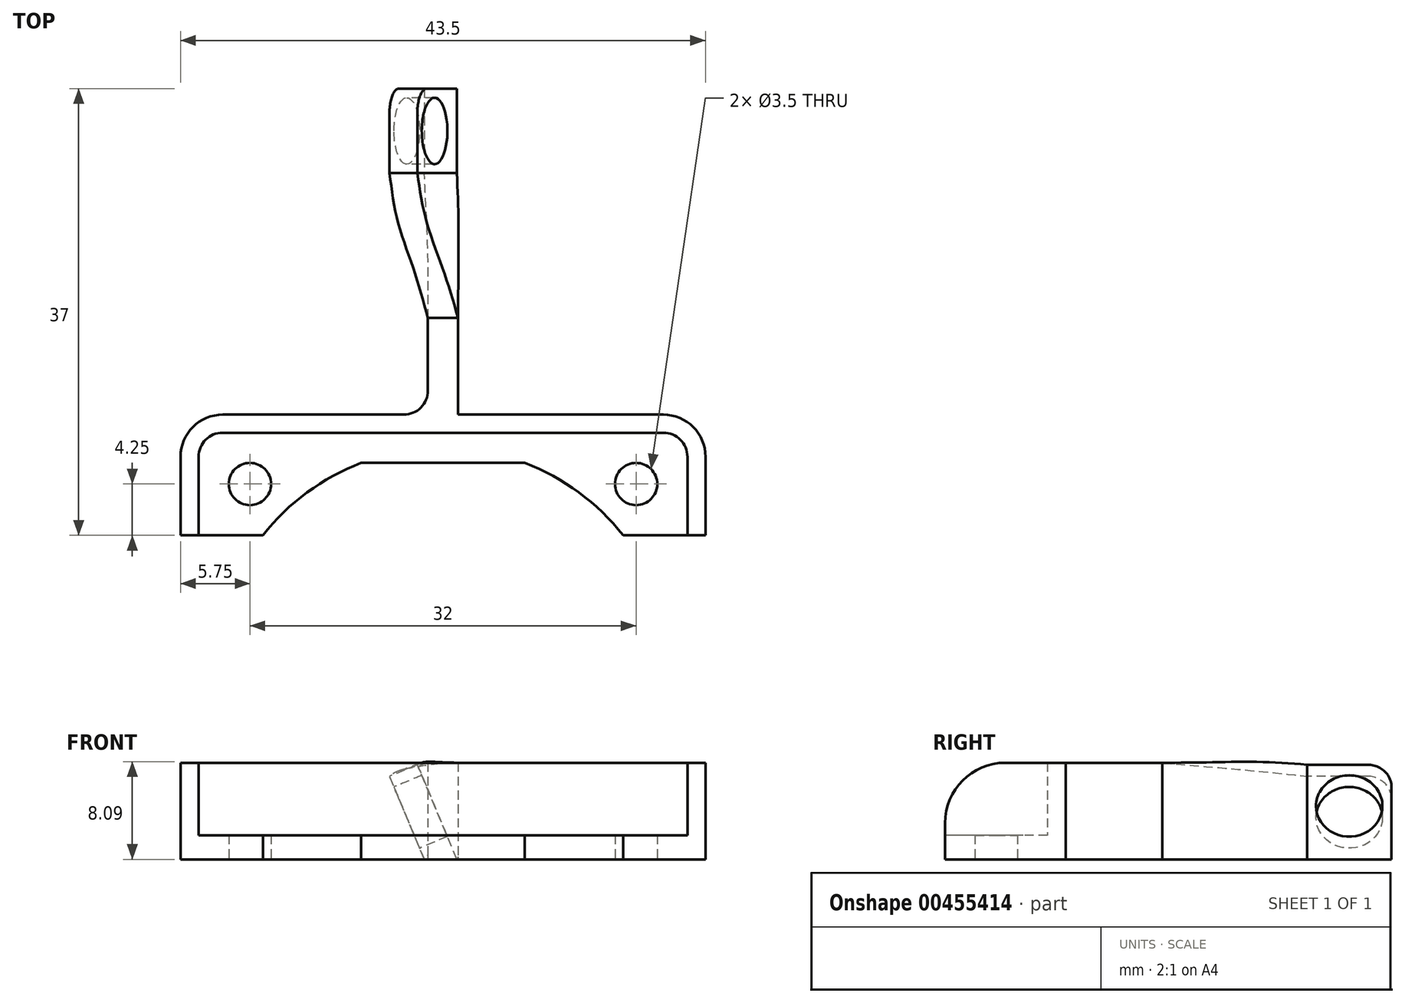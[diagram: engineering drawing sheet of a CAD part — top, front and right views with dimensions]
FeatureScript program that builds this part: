
annotation { "Feature Type Name" : "Feature", "Feature Type Description" : "" }
export const myFeature = defineFeature(function(context is Context, id is Id, definition is map)
    precondition{}
    {
        {
            var Q0;
            Q0=qCreatedBy(makeId("Top.planeOp"),FACE);
            var sketch = newSketch(context, id + "F0", { "sketchPlane" : qUnion([Q0])});
            skCircle(sketch, "E0", {"center": v(0, 0) * mm, "radius": 1.75 * mm});
            skCircle(sketch, "E1", {"center": v(32, 0) * mm, "radius": 1.75 * mm});
            skLineSegment(sketch, "E2", {"start": v(-4.25, 4.25) * mm, "end": v(-4.25, -4.25) * mm});
            skLineSegment(sketch, "E3", {"start": v(36.25, 4.25) * mm, "end": v(36.25, -4.25) * mm});
            skLineSegment(sketch, "E4", {"start": v(-4.25, 4.25) * mm, "end": v(36.25, 4.25) * mm});
            skLineSegment(sketch, "E5", {"start": v(-4.25, -4.25) * mm, "end": v(1.07, -4.25) * mm});
            skLineSegment(sketch, "E6", {"start": v(30.93, -4.25) * mm, "end": v(36.25, -4.25) * mm});
            skArc(sketch, "E7", {"start": v(30.93, -4.25) * mm, "mid": v(27.26, -0.7) * mm, "end": v(22.78, 1.75) * mm});
            skPoint(sketch, "E8.orphan", {"position": v(5.05, -4.25) * mm});
            skPoint(sketch, "E9.orphan", {"position": v(25.59, -4.25) * mm});
            skLineSegment(sketch, "E10", {"start": v(9.22, 1.75) * mm, "end": v(22.78, 1.75) * mm});
            skArc(sketch, "E11.trimOffspring", {"start": v(9.22, 1.75) * mm, "mid": v(4.74, -0.7) * mm, "end": v(1.07, -4.25) * mm});
            skSolve(sketch);
        }
        {
            var Q0;
            Q0=makeQuery(id+"F0.imprint","IMPRINT",FACE,{"disambiguationData":[TD([[makeQuery(id+"F0.imprint","IMPRINT",EDGE,{"derivedFrom":sQuery(id+"F0.wireOp",EDGE,"E0")}),-1.0]])]});
            extrude(context, id + "F1", {"entities" : qUnion([Q0]), "depth" : 2 * mm});
        }
        {
            var Q0;
            Q0=makeQuery(id+"F1.opExtrude","SWEPT_EDGE",EDGE,{"disambiguationData":[OSD([sQuery(id+"F0.wireOp",EDGE,"E3"),sQuery(id+"F0.wireOp",EDGE,"E4")])]});
            var Q1;
            Q1=makeQuery(id+"F1.opExtrude","SWEPT_EDGE",EDGE,{"disambiguationData":[OSD([sQuery(id+"F0.wireOp",EDGE,"E2"),sQuery(id+"F0.wireOp",EDGE,"E4")])]});
            fillet(context, id + "F2", {"entities" : qUnion([Q0, Q1]), "radius" : 2 * mm, "tangentPropagation" : true, "allowEdgeOverflow" : false});
        }
        {
            var Q0;
            Q0=qCreatedBy(makeId("Top.planeOp"),FACE);
            var sketch = newSketch(context, id + "F3", { "sketchPlane" : qUnion([Q0])});
            skLineSegment(sketch, "E12.0", {"start": v(-5.75, 2.25) * mm, "end": v(-5.75, -4.25) * mm});
            skLineSegment(sketch, "E12.1", {"start": v(37.75, 2.25) * mm, "end": v(37.75, -4.25) * mm});
            skArc(sketch, "E12.2", {"start": v(37.75, 2.25) * mm, "mid": v(36.72, 4.72) * mm, "end": v(34.25, 5.75) * mm});
            skLineSegment(sketch, "E12.3", {"start": v(-2.25, 5.75) * mm, "end": v(34.25, 5.75) * mm});
            skArc(sketch, "E12.4", {"start": v(-2.25, 5.75) * mm, "mid": v(-4.72, 4.72) * mm, "end": v(-5.75, 2.25) * mm});
            skLineSegment(sketch, "E13.0", {"start": v(-4.25, 2.25) * mm, "end": v(-4.25, -4.25) * mm});
            skLineSegment(sketch, "E13.1", {"start": v(36.25, 2.25) * mm, "end": v(36.25, -4.25) * mm});
            skArc(sketch, "E13.2", {"start": v(36.25, 2.25) * mm, "mid": v(35.66, 3.66) * mm, "end": v(34.25, 4.25) * mm});
            skLineSegment(sketch, "E13.3", {"start": v(-2.25, 4.25) * mm, "end": v(34.25, 4.25) * mm});
            skArc(sketch, "E13.4", {"start": v(-2.25, 4.25) * mm, "mid": v(-3.66, 3.66) * mm, "end": v(-4.25, 2.25) * mm});
            skLineSegment(sketch, "E14", {"start": v(-5.75, -4.25) * mm, "end": v(-4.25, -4.25) * mm});
            skLineSegment(sketch, "E15", {"start": v(36.25, -4.25) * mm, "end": v(37.75, -4.25) * mm});
            skSolve(sketch);
        }
        {
            var Q0;
            Q0=makeQuery(id+"F3.imprint","IMPRINT",FACE,{"disambiguationData":[TD([[makeQuery(id+"F3.imprint","IMPRINT",EDGE,{"derivedFrom":sQuery(id+"F3.wireOp",EDGE,"E12.0")}),1.0]])]});
            extrude(context, id + "F4", {"entities" : qUnion([Q0]), "operationType" : NewBodyOperationType.ADD, "depth" : 8 * mm});
        }
        {
            var Q0;
            Q0=makeQuery(id+"F4.opExtrude","SWEPT_FACE",FACE,{"disambiguationData":[OSD([sQuery(id+"F3.wireOp",EDGE,"E12.1")])]});
            var Q1;
            Q1=makeQuery(id+"F4.opExtrude","SWEPT_FACE",FACE,{"disambiguationData":[OSD([sQuery(id+"F3.wireOp",EDGE,"E12.0")])]});
            cPlane(context, id + "F5", {"entities" : qUnion([Q0, Q1]), "cplaneType" : CPlaneType.MID_PLANE, "offset" : 25 * mm, "width" : 150 * mm, "height" : 150 * mm});
        }
        {
            var Q0;
            Q0=makeQuery(id+"F4.opExtrude","CAP_EDGE",EDGE,{"disambiguationData":[OSD([sQuery(id+"F3.wireOp",EDGE,"E14")])],"isStart":false});
            var Q1;
            Q1=makeQuery(id+"F4.opExtrude","CAP_EDGE",EDGE,{"disambiguationData":[OSD([sQuery(id+"F3.wireOp",EDGE,"E15")])],"isStart":false});
            fillet(context, id + "F6", {"entities" : qUnion([Q0, Q1]), "radius" : 5 * mm, "tangentPropagation" : true, "allowEdgeOverflow" : false});
        }
        {
            var Q0;
            Q0=makeQuery(id+"F4.opExtrude","SWEPT_FACE",FACE,{"disambiguationData":[OSD([sQuery(id+"F3.wireOp",EDGE,"E12.3")])]});
            cPlane(context, id + "F7", {"entities" : qUnion([Q0]), "cplaneType" : CPlaneType.OFFSET, "offset" : 8 * mm, "width" : 150 * mm, "height" : 150 * mm});
        }
        {
            var Q0;
            Q0=makeQuery(id+"F4.opExtrude","SWEPT_FACE",FACE,{"disambiguationData":[OSD([sQuery(id+"F3.wireOp",EDGE,"E12.3")])]});
            var sketch = newSketch(context, id + "F8", { "sketchPlane" : qUnion([Q0])});
            skLineSegment(sketch, "E16.bottom", {"start": v(-17.25, 8) * mm, "end": v(-14.75, 8) * mm});
            skLineSegment(sketch, "E16.top", {"start": v(-17.25, 0) * mm, "end": v(-14.75, 0) * mm});
            skLineSegment(sketch, "E16.left", {"start": v(-17.25, 8) * mm, "end": v(-17.25, 0) * mm});
            skLineSegment(sketch, "E16.right", {"start": v(-14.75, 8) * mm, "end": v(-14.75, 0) * mm});
            skSolve(sketch);
        }
        {
            var Q0;
            Q0=makeQuery(id+"F8.imprint","IMPRINT",FACE,{"disambiguationData":[TD([[makeQuery(id+"F8.imprint","IMPRINT",EDGE,{"derivedFrom":sQuery(id+"F8.wireOp",EDGE,"E16.bottom")}),1.0]])]});
            extrude(context, id + "F9", {"entities" : qUnion([Q0]), "operationType" : NewBodyOperationType.ADD, "depth" : 8 * mm});
        }
        {
            var Q0;
            Q0=makeQuery(id+"F9.opExtrude","CAP_EDGE",EDGE,{"disambiguationData":[OSD([sQuery(id+"F8.wireOp",EDGE,"E16.right")])],"isStart":true});
            var Q1;
            Q1=makeQuery(id+"F9.opExtrude","CAP_EDGE",EDGE,{"disambiguationData":[OSD([sQuery(id+"F8.wireOp",EDGE,"E16.left")])],"isStart":true});
            fillet(context, id + "F10", {"entities" : qUnion([Q0, Q1]), "radius" : 2 * mm, "tangentPropagation" : true, "allowEdgeOverflow" : false});
        }
        {
            var Q0;
            Q0=qCreatedBy(id+"F7.planeOp",FACE);
            cPlane(context, id + "F11", {"entities" : qUnion([Q0]), "cplaneType" : CPlaneType.OFFSET, "offset" : 4 * mm, "width" : 150 * mm, "height" : 150 * mm});
        }
        {
            var Q0;
            Q0=qCreatedBy(id+"F11.planeOp",FACE);
            var sketch = newSketch(context, id + "F12", { "sketchPlane" : qUnion([Q0])});
            skLineSegment(sketch, "E17", {"start": v(-16.01, 8.03) * mm, "end": v(-17.27, 0) * mm});
            skLineSegment(sketch, "E18", {"start": v(-17.27, 0) * mm, "end": v(-14.77, 0) * mm});
            skLineSegment(sketch, "E19", {"start": v(-14.77, 0) * mm, "end": v(-13.57, 7.65) * mm});
            skLineSegment(sketch, "E20", {"start": v(-16.01, 8.03) * mm, "end": v(-13.57, 7.65) * mm});
            skSolve(sketch);
        }
        {
            var Q0;
            Q0=qCreatedBy(id+"F11.planeOp",FACE);
            cPlane(context, id + "F13", {"entities" : qUnion([Q0]), "cplaneType" : CPlaneType.OFFSET, "offset" : 4 * mm, "width" : 150 * mm, "height" : 150 * mm});
        }
        {
            var Q0;
            Q0=qCreatedBy(id+"F13.planeOp",FACE);
            var sketch = newSketch(context, id + "F14", { "sketchPlane" : qUnion([Q0])});
            skLineSegment(sketch, "E21", {"start": v(-17.28, 0) * mm, "end": v(-14.63, 8.08) * mm});
            skLineSegment(sketch, "E22", {"start": v(-14.63, 8.08) * mm, "end": v(-12.26, 7.3) * mm});
            skLineSegment(sketch, "E23", {"start": v(-12.26, 7.3) * mm, "end": v(-14.65, 0) * mm});
            skLineSegment(sketch, "E24", {"start": v(-17.28, 0) * mm, "end": v(-14.65, 0) * mm});
            skSolve(sketch);
        }
        {
            var Q0;
            Q0=qCreatedBy(id+"F13.planeOp",FACE);
            cPlane(context, id + "F15", {"entities" : qUnion([Q0]), "cplaneType" : CPlaneType.OFFSET, "offset" : 4 * mm, "width" : 150 * mm, "height" : 150 * mm});
        }
        {
            var Q0;
            Q0=qCreatedBy(id+"F15.planeOp",FACE);
            var sketch = newSketch(context, id + "F16", { "sketchPlane" : qUnion([Q0])});
            skLineSegment(sketch, "E25", {"start": v(-17.15, 0) * mm, "end": v(-13.87, 7.84) * mm});
            skLineSegment(sketch, "E26", {"start": v(-13.87, 7.84) * mm, "end": v(-11.57, 6.88) * mm});
            skLineSegment(sketch, "E27", {"start": v(-11.57, 6.88) * mm, "end": v(-14.44, 0) * mm});
            skLineSegment(sketch, "E28", {"start": v(-14.44, 0) * mm, "end": v(-17.15, 0) * mm});
            skSolve(sketch);
        }
        {
            var Q1;
            Q1=makeQuery(id+"F9.opExtrude","CAP_FACE",FACE,{"disambiguationData":[OSD([sQuery(id+"F8.wireOp",EDGE,"E16.bottom"),sQuery(id+"F8.wireOp",EDGE,"E16.top"),sQuery(id+"F8.wireOp",EDGE,"E16.left"),sQuery(id+"F8.wireOp",EDGE,"E16.right")])],"isStart":false});
            var Q2;
            Q2=makeQuery(id+"F12.imprint","IMPRINT",FACE,{"disambiguationData":[TD([[makeQuery(id+"F12.imprint","IMPRINT",EDGE,{"derivedFrom":sQuery(id+"F12.wireOp",EDGE,"E17")}),1.0]])]});
            var Q3;
            Q3=makeQuery(id+"F14.imprint","IMPRINT",FACE,{"disambiguationData":[TD([[makeQuery(id+"F14.imprint","IMPRINT",EDGE,{"derivedFrom":sQuery(id+"F14.wireOp",EDGE,"E21")}),-1.0]])]});
            var Q4;
            Q4=makeQuery(id+"F16.imprint","IMPRINT",FACE,{"disambiguationData":[TD([[makeQuery(id+"F16.imprint","IMPRINT",EDGE,{"derivedFrom":sQuery(id+"F16.wireOp",EDGE,"E25")}),-1.0]])]});
            loft(context, id + "F17", {"operationType" : NewBodyOperationType.ADD, "sheetProfilesArray" : [{ "sheetProfileEntities" : qUnion([Q1]) }, { "sheetProfileEntities" : qUnion([Q2]) }, { "sheetProfileEntities" : qUnion([Q3]) }, { "sheetProfileEntities" : qUnion([Q4]) }]});
        }
        {
            var Q0;
            Q0=makeQuery(id+"F17.opLoft","CAP_FACE",FACE,{"disambiguationData":[OSD([makeQuery(id+"F16.imprint","IMPRINT",FACE,{"disambiguationData":[TD([[makeQuery(id+"F16.imprint","IMPRINT",EDGE,{"derivedFrom":sQuery(id+"F16.wireOp",EDGE,"E25")}),-1.0]])]})])],"isStart":true});
            extrude(context, id + "F18", {"entities" : qUnion([Q0]), "operationType" : NewBodyOperationType.ADD, "depth" : 7 * mm});
        }
        {
            var Q0;
            Q0=makeQuery(id+"F18.opExtrude","CAP_EDGE",EDGE,{"disambiguationData":[OSD([sQuery(id+"F16.wireOp",EDGE,"E25"),sQuery(id+"F16.wireOp",EDGE,"E26"),sQuery(id+"F16.wireOp",EDGE,"E27")])],"isStart":false});
            fillet(context, id + "F19", {"entities" : qUnion([Q0]), "radius" : 2 * mm, "tangentPropagation" : true, "allowEdgeOverflow" : false});
        }
        {
            var Q0;
            Q0=makeQuery(id+"F18.opExtrude","SWEPT_FACE",FACE,{"disambiguationData":[OSD([sQuery(id+"F16.wireOp",EDGE,"E26"),sQuery(id+"F16.wireOp",EDGE,"E27"),sQuery(id+"F16.wireOp",EDGE,"E28")])]});
            var sketch = newSketch(context, id + "F20", { "sketchPlane" : qUnion([Q0])});
            skCircle(sketch, "E29", {"center": v(-29.25, -1.81) * mm, "radius": 2.75 * mm});
            skSolve(sketch);
        }
        {
            var Q0;
            Q0=sQuery(id+"F20.wireOp",VERTEX,"E29.center");
            var Q1;
            Q1=makeQuery(id+"F1.opExtrude","SWEPT_BODY",BODY,{"disambiguationData":[OSD([sQuery(id+"F0.wireOp",EDGE,"E0"),sQuery(id+"F0.wireOp",EDGE,"E1"),sQuery(id+"F0.wireOp",EDGE,"E2"),sQuery(id+"F0.wireOp",EDGE,"E3"),sQuery(id+"F0.wireOp",EDGE,"E4"),sQuery(id+"F0.wireOp",EDGE,"E5"),sQuery(id+"F0.wireOp",EDGE,"E6"),sQuery(id+"F0.wireOp",EDGE,"E7"),sQuery(id+"F0.wireOp",EDGE,"E10"),sQuery(id+"F0.wireOp",EDGE,"E11.trimOffspring")])]});
            hole(context, id + "F21", {"style" : HoleStyle.SIMPLE, "endStyle" : HoleEndStyle.THROUGH, "standardTappedOrClearance" : lookupTablePath({ "standard" : "ISO", "fit" : "Normal", "size" : "M5", "type" : "Clearance" }), "standardBlindInLast" : lookupTablePath({ "fit" : "Standard", "standard" : "ISO", "size" : "M5", "type" : "Clearance" }), "holeDiameter" : 5.5 * mm, "isTappedThrough" : true, "tappedDepth" : 12 * mm, "tapClearance" : 3, "locations" : qUnion([Q0]), "scope" : qUnion([Q1])});
        }
    });
